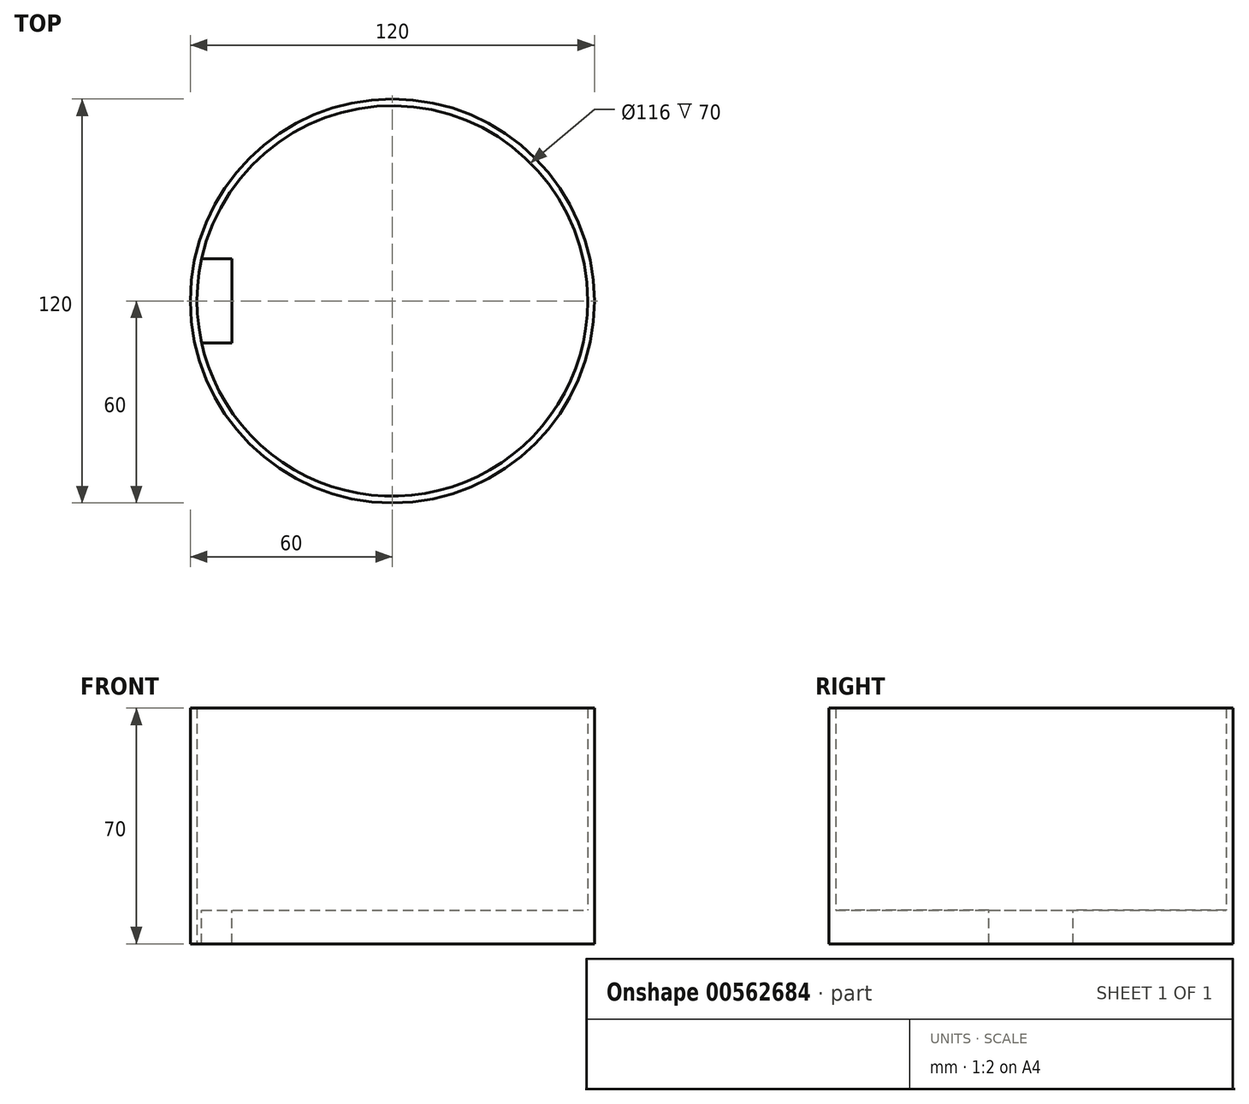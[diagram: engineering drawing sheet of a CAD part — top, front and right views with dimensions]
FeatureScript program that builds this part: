
annotation { "Feature Type Name" : "Feature", "Feature Type Description" : "" }
export const myFeature = defineFeature(function(context is Context, id is Id, definition is map)
    precondition{}
    {
        {
            var Q0;
            Q0=qCreatedBy(makeId("Top.planeOp"),FACE);
            var sketch = newSketch(context, id + "F0", { "sketchPlane" : qUnion([Q0])});
            skCircle(sketch, "E0", {"center": v(0, 0) * mm, "radius": 60 * mm});
            skCircle(sketch, "E1", {"center": v(0, 0) * mm, "radius": 58 * mm});
            skSolve(sketch);
        }
        {
            var Q0;
            Q0=makeQuery(id+"F0.imprint","IMPRINT",FACE,{"disambiguationData":[TD([[makeQuery(id+"F0.imprint","IMPRINT",EDGE,{"derivedFrom":sQuery(id+"F0.wireOp",EDGE,"E1")}),1.0]])]});
            extrude(context, id + "F1", {"entities" : qUnion([Q0]), "depth" : 10 * mm, "offsetDistance" : 25.4 * mm});
        }
        {
            var Q0;
            Q0=makeQuery(id+"F0.imprint","IMPRINT",FACE,{"disambiguationData":[TD([[makeQuery(id+"F0.imprint","IMPRINT",EDGE,{"derivedFrom":sQuery(id+"F0.wireOp",EDGE,"E0")}),1.0]])]});
            extrude(context, id + "F2", {"entities" : qUnion([Q0]), "operationType" : NewBodyOperationType.ADD, "depth" : 70 * mm, "offsetDistance" : 25.4 * mm});
        }
        {
            var Q0;
            Q0=makeQuery(id+"F1.opExtrude","CAP_FACE",FACE,{"disambiguationData":[OSD([sQuery(id+"F0.wireOp",EDGE,"E1")])],"isStart":false});
            var sketch = newSketch(context, id + "F3", { "sketchPlane" : qUnion([Q0])});
            skCircle(sketch, "E2.0", {"center": v(0, 0) * mm, "radius": 58 * mm});
            skLineSegment(sketch, "E3", {"start": v(-56.64, -12.5) * mm, "end": v(-47.64, -12.5) * mm});
            skLineSegment(sketch, "E4", {"start": v(-47.64, -12.5) * mm, "end": v(-47.64, 12.5) * mm});
            skLineSegment(sketch, "E5", {"start": v(-47.64, 12.5) * mm, "end": v(-56.64, 12.5) * mm});
            skSolve(sketch);
        }
        {
            var Q0;
            {var subQ0=sQuery(id+"F3.wireOp",EDGE,"E3");Q0=makeQuery(id+"F3.imprint","IMPRINT",FACE,{"disambiguationData":[TD([[makeQuery(id+"F3.imprint","IMPRINT",EDGE,{"derivedFrom":subQ0}),1.0]])]});}
            extrude(context, id + "F4", {"entities" : qUnion([Q0]), "operationType" : NewBodyOperationType.REMOVE, "endBound" : BoundingType.THROUGH_ALL, "oppositeDirection" : true, "depth" : 25.4 * mm, "offsetDistance" : 25.4 * mm});
        }
    });
